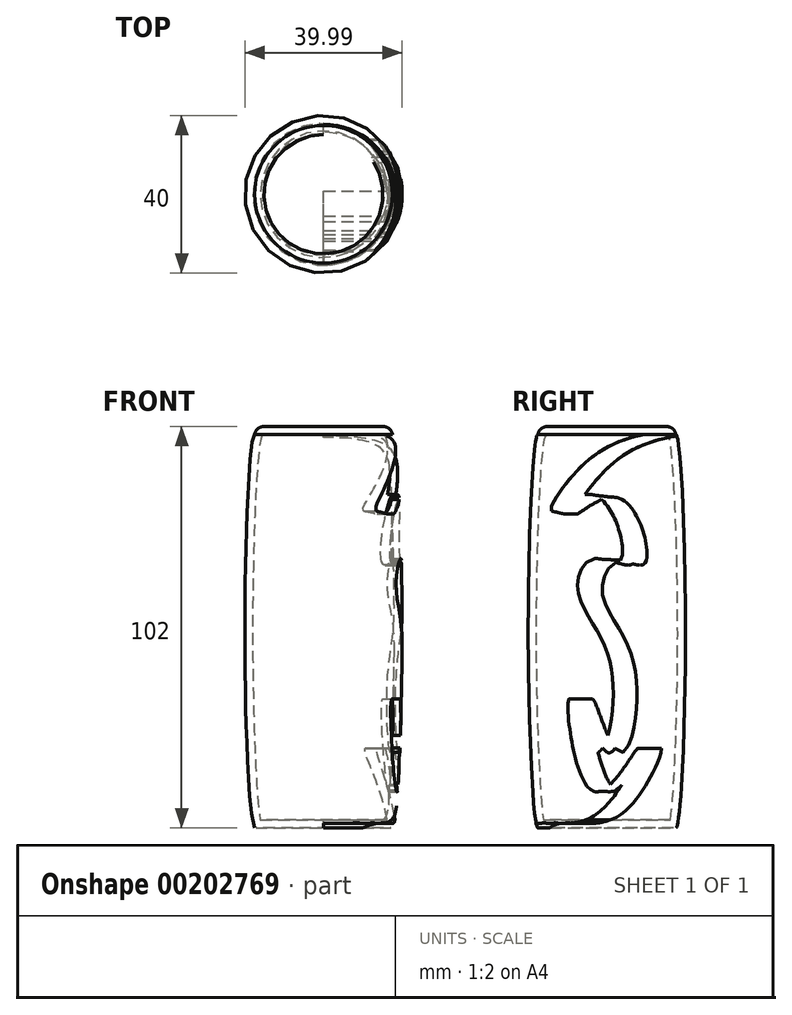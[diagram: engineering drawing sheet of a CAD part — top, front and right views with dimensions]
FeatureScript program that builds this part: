
annotation { "Feature Type Name" : "Feature", "Feature Type Description" : "" }
export const myFeature = defineFeature(function(context is Context, id is Id, definition is map)
    precondition{}
    {
        {
            assignVariable(context, id + "F0", {"name" : "Diam1", "anyValue" : 35});
        }
        {
            assignVariable(context, id + "F1", {"name" : "Height1", "anyValue" : 50});
        }
        {
            assignVariable(context, id + "F2", {"name" : "Diam2", "anyValue" : 40});
        }
        {
            assignVariable(context, id + "F3", {"name" : "Height2", "anyValue" : 50});
        }
        {
            assignVariable(context, id + "F4", {"name" : "Diam3", "anyValue" : 35});
        }
        {
            assignVariable(context, id + "F5", {"name" : "Thickness", "anyValue" : 2});
        }
        {
            var Q0;
            Q0=qCreatedBy(makeId("Top.planeOp"),FACE);
            var sketch = newSketch(context, id + "F6", { "sketchPlane" : qUnion([Q0])});
            skCircle(sketch, "E0.0", {"center": v(0, 0) * mm, "radius": 17.5 * mm});
            skSolve(sketch);
        }
        {
            var Q0;
            Q0=qCreatedBy(makeId("Top.planeOp"),FACE);
            cPlane(context, id + "F7", {"entities" : qUnion([Q0]), "cplaneType" : CPlaneType.OFFSET, "offset" : (getVariable(context, 'Height1')) * mm, "width" : 150 * mm, "height" : 150 * mm});
        }
        {
            var Q0;
            Q0=qCreatedBy(id+"F7.planeOp",FACE);
            var sketch = newSketch(context, id + "F8", { "sketchPlane" : qUnion([Q0])});
            skCircle(sketch, "E1", {"center": v(0, 0) * mm, "radius": 20 * mm});
            skPoint(sketch, "E2", {"position": v(-20, 0) * mm});
            skPoint(sketch, "E3", {"position": v(20, 0) * mm});
            skPoint(sketch, "E4", {"position": v(0, -20) * mm});
            skPoint(sketch, "E5", {"position": v(0, 20) * mm});
            skSolve(sketch);
        }
        {
            var Q0;
            Q0=qCreatedBy(id+"F7.planeOp",FACE);
            cPlane(context, id + "F9", {"entities" : qUnion([Q0]), "cplaneType" : CPlaneType.OFFSET, "offset" : (getVariable(context, 'Height2')) * mm, "width" : 150 * mm, "height" : 150 * mm});
        }
        {
            var Q0;
            Q0=qCreatedBy(id+"F9.planeOp",FACE);
            var sketch = newSketch(context, id + "F10", { "sketchPlane" : qUnion([Q0])});
            skCircle(sketch, "E6", {"center": v(0, 0) * mm, "radius": 17.5 * mm});
            skSolve(sketch);
        }
        {
            var Q0;
            Q0 = qSketchRegion(id + "F6", true);
            var Q1;
            Q1 = qSketchRegion(id + "F8", true);
            var Q2;
            Q2 = qSketchRegion(id + "F10", true);
            loft(context, id + "F11", {"startCondition" : LoftEndDerivativeType.TANGENT_TO_PROFILE, "startMagnitude" : 1, "endCondition" : LoftEndDerivativeType.TANGENT_TO_PROFILE, "endMagnitude" : 1, "sheetProfilesArray" : [{ "sheetProfileEntities" : qUnion([Q0]) }, { "sheetProfileEntities" : qUnion([Q1]) }, { "sheetProfileEntities" : qUnion([Q2]) }]});
        }
        {
            var Q0;
            Q0=makeQuery(id+"F11.opLoft","CAP_FACE",FACE,{"disambiguationData":[OSD([makeQuery(id+"F10.imprint","IMPRINT",FACE,{"disambiguationData":[TD([[makeQuery(id+"F10.imprint","IMPRINT",EDGE,{"derivedFrom":sQuery(id+"F10.wireOp",EDGE,"E6")}),1.0]])]})])],"isStart":true});
            shell(context, id + "F12", {"entities" : qUnion([Q0]), "thickness" : (getVariable(context, 'Thickness')) * mm});
        }
        {
            var Q0;
            Q0=qCreatedBy(makeId("Right.planeOp"),FACE);
            cPlane(context, id + "F13", {"entities" : qUnion([Q0]), "cplaneType" : CPlaneType.OFFSET, "offset" : 0.5 * (max(max(getVariable(context, 'Diam1'), getVariable(context, 'Diam2')), getVariable(context, 'Diam3'))) * mm, "width" : 150 * mm, "height" : 150 * mm});
        }
        {
            var Q0;
            Q0=qCreatedBy(id+"F13.planeOp",FACE);
            var sketch = newSketch(context, id + "F14", { "sketchPlane" : qUnion([Q0])});
            skFitSpline(sketch, "E7.0", {"points": [v(-17.5, 0) * mm, v(-5.83, 0) * mm, v(5.83, 0) * mm, v(17.5, 0) * mm]});
            skFitSpline(sketch, "E8.0", {"points": [v(-17.5, 100) * mm, v(-5.83, 100) * mm, v(5.83, 100) * mm, v(17.5, 100) * mm]});
            skPoint(sketch, "E9.0", {"position": v(20, 50) * mm});
            skPoint(sketch, "E10.0", {"position": v(-20, 50) * mm});
            skFitSpline(sketch, "E11", {"points": [v(-17.5, 0) * mm, v(0, 3.1) * mm, v(10.82, 20.23) * mm, v(0, 9.27) * mm, v(-6.68, 32.73) * mm, v(0, 19.27) * mm, v(4.13, 40.45) * mm, v(-4.13, 59.55) * mm, v(0, 67.64) * mm, v(6.68, 67.28) * mm, v(0, 83.82) * mm, v(-10.82, 79.78) * mm, v(0, 93.82) * mm, v(17.5, 100) * mm], "startDerivative": vector(111.88, 111.88) * mm, "endDerivative": vector(108.34, 15.77) * mm});
            skLineSegment(sketch, "E12", {"start": v(-17.5, 0) * mm, "end": v(-14.5, 0) * mm});
            skLineSegment(sketch, "E13", {"start": v(17.5, 100) * mm, "end": v(20.5, 100) * mm});
            skLineSegment(sketch, "E14", {"start": v(-17.5, 0) * mm, "end": v(-20.5, 0) * mm});
            skLineSegment(sketch, "E15", {"start": v(17.5, 100) * mm, "end": v(14.5, 100) * mm});
            skFitSpline(sketch, "E16", {"points": [v(-14.5, 0) * mm, v(3, 3.1) * mm, v(13.82, 20.23) * mm, v(3, 9.27) * mm, v(-3.68, 32.73) * mm, v(3, 19.27) * mm, v(7.13, 40.45) * mm, v(-1.13, 59.55) * mm, v(3, 67.64) * mm, v(9.68, 67.28) * mm, v(3, 83.82) * mm, v(-7.82, 79.78) * mm, v(3, 93.82) * mm, v(20.5, 100) * mm], "startDerivative": vector(111.88, 111.88) * mm, "endDerivative": vector(108.34, 15.77) * mm});
            skFitSpline(sketch, "E17", {"points": [v(-20.5, 0) * mm, v(-3.28, 3.1) * mm, v(7.82, 20.23) * mm, v(-3.27, 9.27) * mm, v(-9.68, 32.73) * mm, v(-3.27, 19.27) * mm, v(1.13, 40.45) * mm, v(-7.4, 60.3) * mm, v(-3.27, 68.39) * mm, v(3.42, 68.02) * mm, v(-3.28, 84.57) * mm, v(-14.08, 80.52) * mm, v(-3.32, 94.57) * mm, v(14.23, 100.75) * mm], "startDerivative": vector(111.88, 111.88) * mm, "endDerivative": vector(108.38, 15.62) * mm});
            skLineSegment(sketch, "E18", {"start": v(-9.68, 32.73) * mm, "end": v(-3.68, 32.73) * mm});
            skLineSegment(sketch, "E19", {"start": v(7.82, 20.23) * mm, "end": v(13.82, 20.23) * mm});
            skLineSegment(sketch, "E20", {"start": v(-3.27, 9.27) * mm, "end": v(3, 9.27) * mm});
            skLineSegment(sketch, "E21", {"start": v(-3.27, 68.39) * mm, "end": v(3.42, 68.02) * mm});
            skLineSegment(sketch, "E22", {"start": v(9.68, 67.28) * mm, "end": v(0, 67.64) * mm});
            skLineSegment(sketch, "E23", {"start": v(-3.28, 84.57) * mm, "end": v(3, 83.82) * mm});
            skLineSegment(sketch, "E24", {"start": v(-14.08, 80.52) * mm, "end": v(-10.82, 79.78) * mm});
            skLineSegment(sketch, "E25", {"start": v(-10.82, 79.78) * mm, "end": v(-7.82, 79.78) * mm});
            skSolve(sketch);
        }
        {
            var Q0;
            Q0 = qSketchRegion(id + "F14", true);
            var Q1;
            {var subQ0=sQuery(id+"F14.wireOp",EDGE,"E22");var subQ1=sQuery(id+"F14.wireOp",EDGE,"E11");var subQ2=makeQuery(id+"F14.imprint","INTERSECT",VERTEX,{"disambiguationData":[OD(1.0)],"derivedFrom":[subQ1,subQ0]});Q1=makeQuery(id+"F14.imprint","IMPRINT",FACE,{"disambiguationData":[TD([[makeQuery(id+"F14.imprint","IMPRINT",EDGE,{"disambiguationData":[TD([[subQ2,-1.0]])],"derivedFrom":subQ1}),1.0]])]});}
            var Q2;
            {var subQ0=sQuery(id+"F14.wireOp",EDGE,"E17");var subQ1=sQuery(id+"F14.wireOp",EDGE,"E11");var subQ2=makeQuery(id+"F14.imprint","INTERSECT",VERTEX,{"disambiguationData":[OD(6.0)],"derivedFrom":[subQ1,subQ0]});Q2=makeQuery(id+"F14.imprint","IMPRINT",FACE,{"disambiguationData":[TD([[makeQuery(id+"F14.imprint","IMPRINT",EDGE,{"disambiguationData":[TD([[subQ2,-1.0]])],"derivedFrom":subQ1}),-1.0]])]});}
            var Q3;
            {var subQ0=sQuery(id+"F14.wireOp",EDGE,"E17");var subQ1=sQuery(id+"F14.wireOp",EDGE,"E16");var subQ2=makeQuery(id+"F14.imprint","INTERSECT",VERTEX,{"disambiguationData":[OD(9.0)],"derivedFrom":[subQ1,subQ0]});Q3=makeQuery(id+"F14.imprint","IMPRINT",FACE,{"disambiguationData":[TD([[makeQuery(id+"F14.imprint","IMPRINT",EDGE,{"disambiguationData":[TD([[subQ2,-1.0]])],"derivedFrom":subQ1}),-1.0]])]});}
            var Q4;
            {var subQ0=sQuery(id+"F14.wireOp",EDGE,"E22");var subQ1=sQuery(id+"F14.wireOp",EDGE,"E11");var subQ2=makeQuery(id+"F14.imprint","INTERSECT",VERTEX,{"disambiguationData":[OD(0.0)],"derivedFrom":[subQ1,subQ0]});Q4=makeQuery(id+"F14.imprint","IMPRINT",FACE,{"disambiguationData":[TD([[makeQuery(id+"F14.imprint","IMPRINT",EDGE,{"disambiguationData":[TD([[subQ2,-1.0]])],"derivedFrom":subQ1}),-1.0]])]});}
            var Q5;
            {var subQ0=sQuery(id+"F14.wireOp",EDGE,"E22");var subQ1=sQuery(id+"F14.wireOp",EDGE,"E11");var subQ2=makeQuery(id+"F14.imprint","INTERSECT",VERTEX,{"disambiguationData":[OD(1.0)],"derivedFrom":[subQ1,subQ0]});Q5=makeQuery(id+"F14.imprint","IMPRINT",FACE,{"disambiguationData":[TD([[makeQuery(id+"F14.imprint","IMPRINT",EDGE,{"disambiguationData":[TD([[subQ2,-1.0]])],"derivedFrom":subQ1}),-1.0]])]});}
            var Q6;
            Q6=makeQuery(id+"F12.opShell","OFFSET_FACE",FACE,{"disambiguationData":[OSD([sQuery(id+"F6.wireOp",EDGE,"E0.0"),sQuery(id+"F8.wireOp",EDGE,"E1")])]});
            extrude(context, id + "F15", {"entities" : qUnion([Q0, Q1, Q2, Q3, Q4, Q5]), "operationType" : NewBodyOperationType.REMOVE, "oppositeDirection" : true, "endBoundEntityFace" : qUnion([Q6]), "depth" : (0.5 * max(getVariable(context, 'Diam1'), max(getVariable(context, 'Diam2'), getVariable(context, 'Diam3')))) * mm});
        }
        {
            var Q0;
            Q0=qCreatedBy(id+"F9.planeOp",FACE);
            var sketch = newSketch(context, id + "F16", { "sketchPlane" : qUnion([Q0])});
            skPoint(sketch, "E26.0", {"position": v(-9.13, 14.93) * mm});
            skCircle(sketch, "E27", {"center": v(0, 0) * mm, "radius": 17.5 * mm});
            skSolve(sketch);
        }
        {
            var Q0;
            Q0=makeQuery(id+"F16.imprint","IMPRINT",FACE,{"disambiguationData":[TD([[makeQuery(id+"F16.imprint","IMPRINT",EDGE,{"derivedFrom":sQuery(id+"F16.wireOp",EDGE,"E27")}),1.0]])]});
            extrude(context, id + "F17", {"entities" : qUnion([Q0]), "operationType" : NewBodyOperationType.ADD, "depth" : (getVariable(context, 'Thickness')) * mm});
        }
        {
            var Q0;
            Q0=makeQuery(id+"F17.opExtrude","CAP_FACE",FACE,{"disambiguationData":[OSD([sQuery(id+"F16.wireOp",EDGE,"E27")])],"isStart":false});
            fillet(context, id + "F18", {"entities" : qUnion([Q0]), "radius" : (getVariable(context, 'Thickness') * 1.2) * mm, "tangentPropagation" : true, "allowEdgeOverflow" : false});
        }
    });
